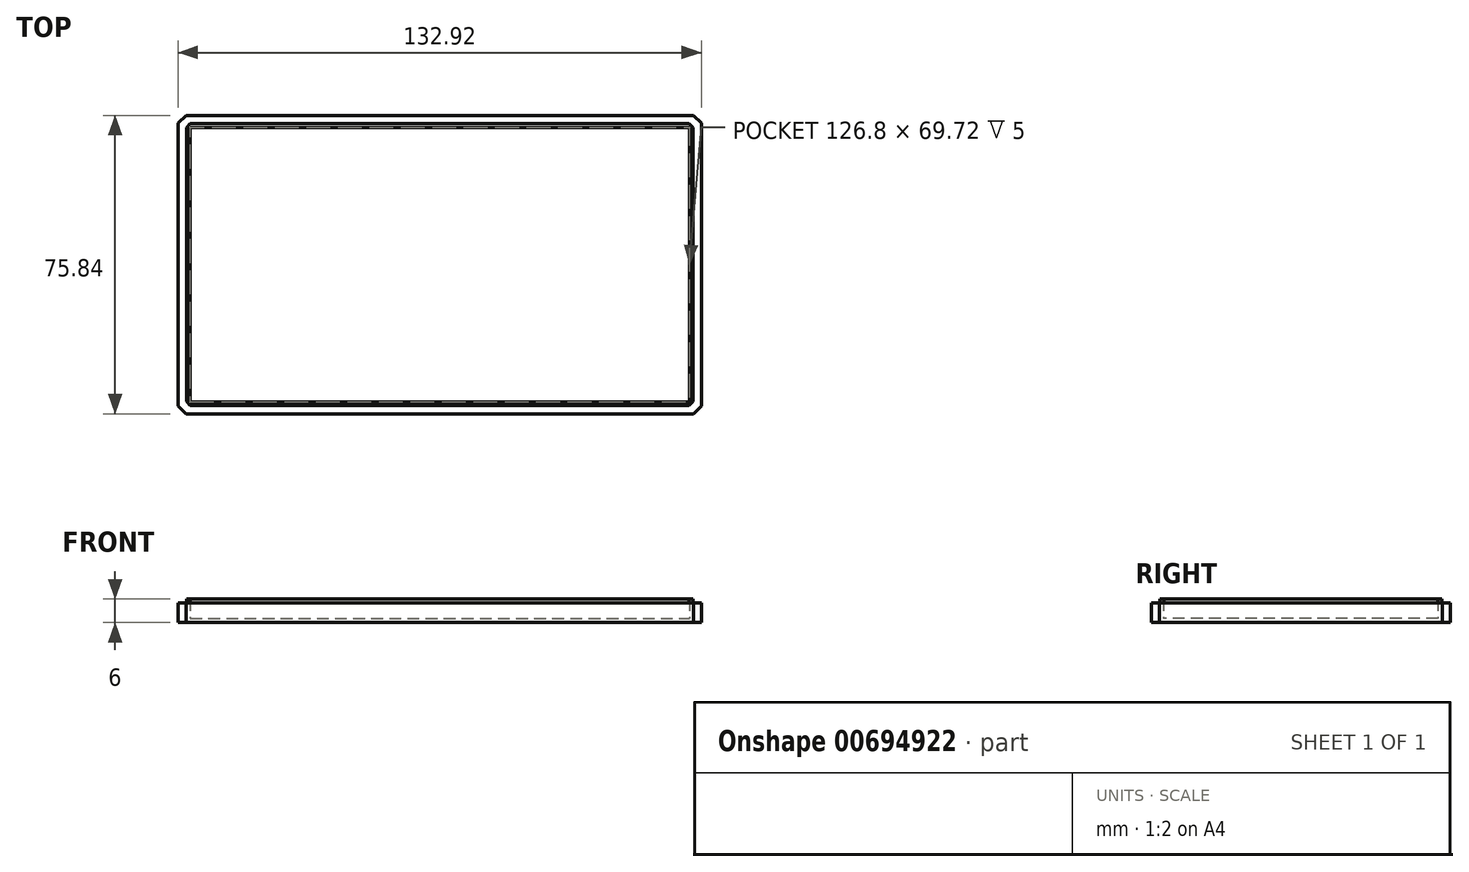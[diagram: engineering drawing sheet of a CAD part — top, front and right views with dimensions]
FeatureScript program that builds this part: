
annotation { "Feature Type Name" : "Feature", "Feature Type Description" : "" }
export const myFeature = defineFeature(function(context is Context, id is Id, definition is map)
    precondition{}
    {
        {
            var Q0;
            Q0=qCreatedBy(makeId("Top.planeOp"),FACE);
            var sketch = newSketch(context, id + "F0", { "sketchPlane" : qUnion([Q0])});
            skLineSegment(sketch, "E0.bottom", {"start": v(-56.88, 41.41) * mm, "end": v(76.04, 41.41) * mm});
            skLineSegment(sketch, "E0.top", {"start": v(-56.88, -34.43) * mm, "end": v(76.04, -34.43) * mm});
            skLineSegment(sketch, "E0.left", {"start": v(-56.88, 41.41) * mm, "end": v(-56.88, -34.43) * mm});
            skLineSegment(sketch, "E0.right", {"start": v(76.04, 41.41) * mm, "end": v(76.04, -34.43) * mm});
            skLineSegment(sketch, "E1.bottom", {"start": v(-54.78, 39.31) * mm, "end": v(73.94, 39.31) * mm});
            skLineSegment(sketch, "E1.top", {"start": v(-54.78, -32.33) * mm, "end": v(73.94, -32.33) * mm});
            skLineSegment(sketch, "E1.left", {"start": v(-54.78, 39.31) * mm, "end": v(-54.78, -32.33) * mm});
            skLineSegment(sketch, "E1.right", {"start": v(73.94, 39.31) * mm, "end": v(73.94, -32.33) * mm});
            skLineSegment(sketch, "E2.bottom", {"start": v(-53.82, 38.35) * mm, "end": v(72.98, 38.35) * mm});
            skLineSegment(sketch, "E2.top", {"start": v(-53.82, -31.37) * mm, "end": v(72.98, -31.37) * mm});
            skLineSegment(sketch, "E2.left", {"start": v(-53.82, 38.35) * mm, "end": v(-53.82, -31.37) * mm});
            skLineSegment(sketch, "E2.right", {"start": v(72.98, 38.35) * mm, "end": v(72.98, -31.37) * mm});
            skSolve(sketch);
        }
        {
            var Q0;
            Q0=makeQuery(id+"F0.imprint","IMPRINT",FACE,{"disambiguationData":[TD([[makeQuery(id+"F0.imprint","IMPRINT",EDGE,{"derivedFrom":sQuery(id+"F0.wireOp",EDGE,"E1.bottom")}),-1.0]])]});
            extrude(context, id + "F1", {"entities" : qUnion([Q0]), "depth" : 6 * mm, "offsetDistance" : 25 * mm});
        }
        {
            var Q0;
            Q0=makeQuery(id+"F0.imprint","IMPRINT",FACE,{"disambiguationData":[TD([[makeQuery(id+"F0.imprint","IMPRINT",EDGE,{"derivedFrom":sQuery(id+"F0.wireOp",EDGE,"E0.bottom")}),-1.0]])]});
            extrude(context, id + "F2", {"entities" : qUnion([Q0]), "operationType" : NewBodyOperationType.ADD, "depth" : 5 * mm, "offsetDistance" : 25 * mm});
        }
        {
            var Q0;
            Q0=makeQuery(id+"F0.imprint","IMPRINT",FACE,{"disambiguationData":[TD([[makeQuery(id+"F0.imprint","IMPRINT",EDGE,{"derivedFrom":sQuery(id+"F0.wireOp",EDGE,"E2.bottom")}),-1.0]])]});
            extrude(context, id + "F3", {"entities" : qUnion([Q0]), "operationType" : NewBodyOperationType.ADD, "depth" : 1 * mm, "offsetDistance" : 25 * mm});
        }
        {
            var Q0;
            Q0=makeQuery(id+"F1.opExtrude","SWEPT_BODY",BODY,{"disambiguationData":[OSD([sQuery(id+"F0.wireOp",EDGE,"E1.bottom"),sQuery(id+"F0.wireOp",EDGE,"E1.top"),sQuery(id+"F0.wireOp",EDGE,"E1.left"),sQuery(id+"F0.wireOp",EDGE,"E1.right"),sQuery(id+"F0.wireOp",EDGE,"E2.bottom"),sQuery(id+"F0.wireOp",EDGE,"E2.top"),sQuery(id+"F0.wireOp",EDGE,"E2.left"),sQuery(id+"F0.wireOp",EDGE,"E2.right")])]});
            transform(context, id + "F4", {"entities" : qUnion([Q0]), "transformType" : TransformType.TRANSLATION_3D, "dx" : -10 * mm, "dy" : 0 * mm, "dz" : 0 * mm, "makeCopy" : false});
        }
        {
            var Q0;
            Q0=makeQuery(id+"F1.opExtrude","SWEPT_EDGE",EDGE,{"disambiguationData":[OSD([sQuery(id+"F0.wireOp",EDGE,"E1.top"),sQuery(id+"F0.wireOp",EDGE,"E1.left")])]});
            var Q1;
            Q1=makeQuery(id+"F1.opExtrude","SWEPT_EDGE",EDGE,{"disambiguationData":[OSD([sQuery(id+"F0.wireOp",EDGE,"E1.top"),sQuery(id+"F0.wireOp",EDGE,"E1.right")])]});
            var Q2;
            Q2=makeQuery(id+"F1.opExtrude","SWEPT_EDGE",EDGE,{"disambiguationData":[OSD([sQuery(id+"F0.wireOp",EDGE,"E1.bottom"),sQuery(id+"F0.wireOp",EDGE,"E1.right")])]});
            var Q3;
            Q3=makeQuery(id+"F1.opExtrude","SWEPT_EDGE",EDGE,{"disambiguationData":[OSD([sQuery(id+"F0.wireOp",EDGE,"E1.bottom"),sQuery(id+"F0.wireOp",EDGE,"E1.left")])]});
            chamfer(context, id + "F5", {"entities" : qUnion([Q0, Q1, Q2, Q3]), "width" : 1 * mm, "tangentPropagation" : true});
        }
        {
            var Q0;
            Q0=makeQuery(id+"F2.opExtrude","SWEPT_EDGE",EDGE,{"disambiguationData":[OSD([sQuery(id+"F0.wireOp",EDGE,"E0.bottom"),sQuery(id+"F0.wireOp",EDGE,"E0.left")])]});
            var Q1;
            Q1=makeQuery(id+"F2.opExtrude","SWEPT_EDGE",EDGE,{"disambiguationData":[OSD([sQuery(id+"F0.wireOp",EDGE,"E0.top"),sQuery(id+"F0.wireOp",EDGE,"E0.left")])]});
            var Q2;
            Q2=makeQuery(id+"F2.opExtrude","SWEPT_EDGE",EDGE,{"disambiguationData":[OSD([sQuery(id+"F0.wireOp",EDGE,"E0.top"),sQuery(id+"F0.wireOp",EDGE,"E0.right")])]});
            var Q3;
            Q3=makeQuery(id+"F2.opExtrude","SWEPT_EDGE",EDGE,{"disambiguationData":[OSD([sQuery(id+"F0.wireOp",EDGE,"E0.bottom"),sQuery(id+"F0.wireOp",EDGE,"E0.right")])]});
            chamfer(context, id + "F6", {"entities" : qUnion([Q0, Q1, Q2, Q3]), "width" : 2 * mm, "tangentPropagation" : true});
        }
    });
